# Revit family: Bogen_90_horizontal_ Russia
name_source: partatom
category: Generic Models
revit_build: Autodesk Revit 2015 (Build: 20140606_1530(x64)
units: mm (PartAtom-declared; Revit-internal decimal feet)

## types (7) — shared parameters
Manufacturer = OBO Bettermann
Material = Stainless Steel
URL = http://www.obo-bettermann.com

## per-type parameters (varying)
| type | A | C | GTIN | Manufacturer Art.No. |
| RBL 90 610 FS RU | 98 mm  [stored 0.321522 ft] | 150 mm  [stored 0.492126 ft] | 4012196606092 | 6043092 |
| RBL 90 615 FS RU | 148 mm  [stored 0.485564 ft] | 200 mm  [stored 0.656168 ft] | 4012196649327 | 6043093 |
| RBL 90 620 FS RU | 198 mm  [stored 0.649606 ft] | 250 mm  [stored 0.82021 ft] | 4012196606108 | 6043094 |
| RBL 90 630 FS RU | 298 mm  [stored 0.97769 ft] | 350 mm  [stored 1.14829 ft] | 4012196606115 | 6043096 |
| RBL 90 640 FS RU | 398 mm  [stored 1.30577 ft] | 450 mm  [stored 1.47638 ft] | 4012196625949 | 6043098 |
| RBL 90 650 FS RU | 498 mm  [stored 1.63386 ft] | 550 mm | 4012196625956 | 6043100 |
| RBL 90 660 FS RU | 598 mm  [stored 1.96194 ft] | 650 mm  [stored 2.13255 ft] | 4012196625963 | 6043102 |

note: column(s) folded — value = type name in every type: Article Type

note: [stored X ft] marks values corroborated as IEEE doubles in the binary element streams (Revit-internal decimal feet)

## geometry (parser evidence)
native form markers: Sweep x2
no freeform markers — native parametric forms only
